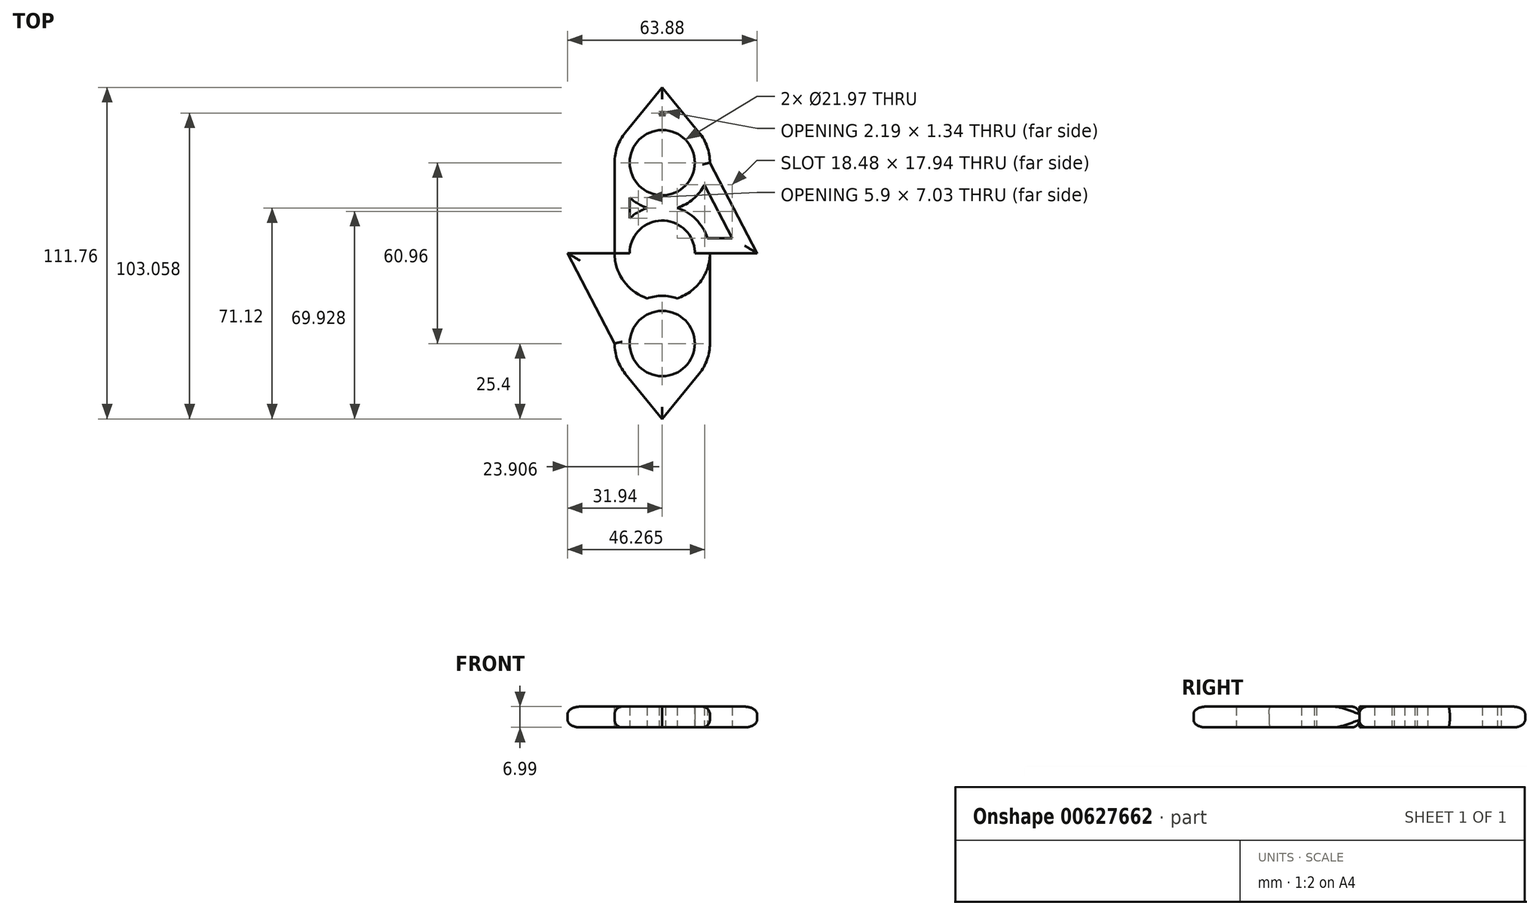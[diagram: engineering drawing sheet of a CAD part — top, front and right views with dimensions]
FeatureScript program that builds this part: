
annotation { "Feature Type Name" : "Feature", "Feature Type Description" : "" }
export const myFeature = defineFeature(function(context is Context, id is Id, definition is map)
    precondition{}
    {
        {
            var Q0;
            Q0=qCreatedBy(makeId("Top.planeOp"),FACE);
            var sketch = newSketch(context, id + "F0", { "sketchPlane" : qUnion([Q0])});
            skCircle(sketch, "E0", {"center": v(0, 0) * mm, "radius": 10.99 * mm});
            skLineSegment(sketch, "E1", {"start": v(0, 0) * mm, "end": v(0, 30.48) * mm});
            skLineSegment(sketch, "E2", {"start": v(0, 0) * mm, "end": v(0, -30.48) * mm});
            skCircle(sketch, "E3", {"center": v(0, -30.48) * mm, "radius": 10.99 * mm});
            skCircle(sketch, "E4", {"center": v(0, 30.48) * mm, "radius": 10.99 * mm});
            skCircle(sketch, "E5", {"center": v(0, 30.48) * mm, "radius": 16.07 * mm});
            skCircle(sketch, "E6", {"center": v(0, 0) * mm, "radius": 16.07 * mm});
            skCircle(sketch, "E7", {"center": v(0, -30.48) * mm, "radius": 16.07 * mm});
            skLineSegment(sketch, "E8", {"start": v(-16.07, 30.48) * mm, "end": v(-16.07, 0) * mm});
            skLineSegment(sketch, "E9", {"start": v(-16.07, 0) * mm, "end": v(-16.07, -30.48) * mm});
            skLineSegment(sketch, "E10", {"start": v(-16.07, 0) * mm, "end": v(16.07, 0) * mm});
            skLineSegment(sketch, "E11", {"start": v(-16.07, 30.48) * mm, "end": v(0, 30.48) * mm});
            skLineSegment(sketch, "E12", {"start": v(0, 30.48) * mm, "end": v(16.07, 30.48) * mm});
            skLineSegment(sketch, "E13", {"start": v(16.07, 30.48) * mm, "end": v(16.07, -30.48) * mm});
            skLineSegment(sketch, "E14", {"start": v(16.07, -30.48) * mm, "end": v(-16.07, -30.48) * mm});
            skLineSegment(sketch, "E15", {"start": v(-16.07, 0) * mm, "end": v(-31.94, 0) * mm});
            skLineSegment(sketch, "E16", {"start": v(-31.94, 0) * mm, "end": v(-16.07, -30.48) * mm});
            skLineSegment(sketch, "E17", {"start": v(16.07, 0) * mm, "end": v(31.94, 0) * mm});
            skLineSegment(sketch, "E18", {"start": v(31.94, 0) * mm, "end": v(16.07, 30.48) * mm});
            skLineSegment(sketch, "E19", {"start": v(0, 30.48) * mm, "end": v(0, 55.88) * mm});
            skLineSegment(sketch, "E20", {"start": v(0, -30.48) * mm, "end": v(0, -55.88) * mm});
            skLineSegment(sketch, "E21", {"start": v(0, 55.88) * mm, "end": v(-12.44, 40.64) * mm});
            skLineSegment(sketch, "E22", {"start": v(0, 55.88) * mm, "end": v(12.44, 40.64) * mm});
            skLineSegment(sketch, "E23", {"start": v(0, -55.88) * mm, "end": v(12.44, -40.64) * mm});
            skLineSegment(sketch, "E24", {"start": v(0, -55.88) * mm, "end": v(-12.44, -40.64) * mm});
            skSolve(sketch);
        }
        {
            var Q0;
            Q0=makeQuery(id+"F0.imprint","IMPRINT",FACE,{"disambiguationData":[TD([[makeQuery(id+"F0.imprint","IMPRINT",EDGE,{"derivedFrom":sQuery(id+"F0.wireOp",EDGE,"E9")}),-1.0]])]});
            var Q1;
            {var subQ0=sQuery(id+"F0.wireOp",EDGE,"E17");Q1=makeQuery(id+"F0.imprint","IMPRINT",FACE,{"disambiguationData":[TD([[makeQuery(id+"F0.imprint","IMPRINT",EDGE,{"derivedFrom":subQ0}),1.0]])]});}
            var Q2;
            {var subQ0=sQuery(id+"F0.wireOp",EDGE,"E22");Q2=makeQuery(id+"F0.imprint","IMPRINT",FACE,{"disambiguationData":[TD([[makeQuery(id+"F0.imprint","IMPRINT",EDGE,{"derivedFrom":subQ0}),-1.0]])]});}
            var Q3;
            {var subQ0=sQuery(id+"F0.wireOp",EDGE,"E21");Q3=makeQuery(id+"F0.imprint","IMPRINT",FACE,{"disambiguationData":[TD([[makeQuery(id+"F0.imprint","IMPRINT",EDGE,{"derivedFrom":subQ0}),1.0]])]});}
            var Q4;
            {var subQ0=sQuery(id+"F0.wireOp",EDGE,"E8");Q4=makeQuery(id+"F0.imprint","IMPRINT",FACE,{"disambiguationData":[TD([[makeQuery(id+"F0.imprint","IMPRINT",EDGE,{"derivedFrom":subQ0}),1.0]])]});}
            var Q5;
            {var subQ0=sQuery(id+"F0.wireOp",EDGE,"E24");Q5=makeQuery(id+"F0.imprint","IMPRINT",FACE,{"disambiguationData":[TD([[makeQuery(id+"F0.imprint","IMPRINT",EDGE,{"derivedFrom":subQ0}),-1.0]])]});}
            var Q6;
            {var subQ0=sQuery(id+"F0.wireOp",EDGE,"E23");Q6=makeQuery(id+"F0.imprint","IMPRINT",FACE,{"disambiguationData":[TD([[makeQuery(id+"F0.imprint","IMPRINT",EDGE,{"derivedFrom":subQ0}),1.0]])]});}
            var Q7;
            {var subQ1=sQuery(id+"F0.wireOp",EDGE,"E5");var subQ3=sQuery(id+"F0.wireOp",EDGE,"E6");var subQ4=makeQuery(id+"F0.imprint","INTERSECT",VERTEX,{"disambiguationData":[OD(1.0)],"derivedFrom":[subQ1,subQ3]});Q7=makeQuery(id+"F0.imprint","IMPRINT",FACE,{"disambiguationData":[TD([[makeQuery(id+"F0.imprint","IMPRINT",EDGE,{"disambiguationData":[TD([[subQ4,-1.0]])],"derivedFrom":subQ1}),-1.0]])]});}
            var Q8;
            {var subQ0=sQuery(id+"F0.wireOp",EDGE,"E9");Q8=makeQuery(id+"F0.imprint","IMPRINT",FACE,{"disambiguationData":[TD([[makeQuery(id+"F0.imprint","IMPRINT",EDGE,{"derivedFrom":subQ0}),1.0]])]});}
            var Q9;
            {var subQ4=sQuery(id+"F0.wireOp",EDGE,"E14");var subQ6=sQuery(id+"F0.wireOp",EDGE,"E3");var subQ7=makeQuery(id+"F0.imprint","INTERSECT",VERTEX,{"disambiguationData":[OD(1.0)],"derivedFrom":[subQ6,subQ4]});Q9=makeQuery(id+"F0.imprint","IMPRINT",FACE,{"disambiguationData":[TD([[makeQuery(id+"F0.imprint","IMPRINT",EDGE,{"disambiguationData":[TD([[subQ7,-1.0]])],"derivedFrom":subQ6}),-1.0]])]});}
            var Q10;
            {var subQ0=sQuery(id+"F0.wireOp",EDGE,"E14");var subQ3=sQuery(id+"F0.wireOp",EDGE,"E3");var subQ4=makeQuery(id+"F0.imprint","INTERSECT",VERTEX,{"disambiguationData":[OD(0.0)],"derivedFrom":[subQ3,subQ0]});Q10=makeQuery(id+"F0.imprint","IMPRINT",FACE,{"disambiguationData":[TD([[makeQuery(id+"F0.imprint","IMPRINT",EDGE,{"disambiguationData":[TD([[subQ4,1.0]])],"derivedFrom":subQ3}),-1.0]])]});}
            var Q11;
            {var subQ3=sQuery(id+"F0.wireOp",EDGE,"E4");var subQ6=sQuery(id+"F0.wireOp",EDGE,"E19");var subQ8=makeQuery(id+"F0.imprint","INTERSECT",VERTEX,{"derivedFrom":[subQ3,subQ6]});Q11=makeQuery(id+"F0.imprint","IMPRINT",FACE,{"disambiguationData":[TD([[makeQuery(id+"F0.imprint","IMPRINT",EDGE,{"disambiguationData":[TD([[subQ8,1.0]])],"derivedFrom":subQ3}),-1.0]])]});}
            var Q12;
            {var subQ3=sQuery(id+"F0.wireOp",EDGE,"E4");var subQ5=sQuery(id+"F0.wireOp",EDGE,"E19");var subQ6=makeQuery(id+"F0.imprint","INTERSECT",VERTEX,{"derivedFrom":[subQ3,subQ5]});Q12=makeQuery(id+"F0.imprint","IMPRINT",FACE,{"disambiguationData":[TD([[makeQuery(id+"F0.imprint","IMPRINT",EDGE,{"disambiguationData":[TD([[subQ6,-1.0]])],"derivedFrom":subQ3}),-1.0]])]});}
            var Q13;
            {var subQ1=sQuery(id+"F0.wireOp",EDGE,"E1");var subQ7=sQuery(id+"F0.wireOp",EDGE,"E0");var subQ8=makeQuery(id+"F0.imprint","INTERSECT",VERTEX,{"derivedFrom":[subQ7,subQ1]});Q13=makeQuery(id+"F0.imprint","IMPRINT",FACE,{"disambiguationData":[TD([[makeQuery(id+"F0.imprint","IMPRINT",EDGE,{"disambiguationData":[TD([[subQ8,1.0]])],"derivedFrom":subQ7}),-1.0]])]});}
            var Q14;
            {var subQ5=sQuery(id+"F0.wireOp",EDGE,"E1");var subQ7=sQuery(id+"F0.wireOp",EDGE,"E0");var subQ8=makeQuery(id+"F0.imprint","INTERSECT",VERTEX,{"derivedFrom":[subQ7,subQ5]});Q14=makeQuery(id+"F0.imprint","IMPRINT",FACE,{"disambiguationData":[TD([[makeQuery(id+"F0.imprint","IMPRINT",EDGE,{"disambiguationData":[TD([[subQ8,-1.0]])],"derivedFrom":subQ7}),-1.0]])]});}
            var Q15;
            {var subQ0=sQuery(id+"F0.wireOp",EDGE,"E10");var subQ7=sQuery(id+"F0.wireOp",EDGE,"E0");var subQ9=makeQuery(id+"F0.imprint","INTERSECT",VERTEX,{"disambiguationData":[OD(1.0)],"derivedFrom":[subQ7,subQ0]});Q15=makeQuery(id+"F0.imprint","IMPRINT",FACE,{"disambiguationData":[TD([[makeQuery(id+"F0.imprint","IMPRINT",EDGE,{"disambiguationData":[TD([[subQ9,-1.0]])],"derivedFrom":subQ7}),-1.0]])]});}
            var Q16;
            {var subQ5=sQuery(id+"F0.wireOp",EDGE,"E10");var subQ7=sQuery(id+"F0.wireOp",EDGE,"E0");var subQ9=makeQuery(id+"F0.imprint","INTERSECT",VERTEX,{"disambiguationData":[OD(0.0)],"derivedFrom":[subQ7,subQ5]});Q16=makeQuery(id+"F0.imprint","IMPRINT",FACE,{"disambiguationData":[TD([[makeQuery(id+"F0.imprint","IMPRINT",EDGE,{"disambiguationData":[TD([[subQ9,1.0]])],"derivedFrom":subQ7}),-1.0]])]});}
            var Q17;
            {var subQ3=sQuery(id+"F0.wireOp",EDGE,"E6");var subQ6=sQuery(id+"F0.wireOp",EDGE,"E1");var subQ9=makeQuery(id+"F0.imprint","INTERSECT",VERTEX,{"derivedFrom":[subQ6,subQ3]});Q17=makeQuery(id+"F0.imprint","IMPRINT",FACE,{"disambiguationData":[TD([[makeQuery(id+"F0.imprint","IMPRINT",EDGE,{"disambiguationData":[TD([[subQ9,-1.0]])],"derivedFrom":subQ6}),1.0]])]});}
            var Q18;
            {var subQ3=sQuery(id+"F0.wireOp",EDGE,"E6");var subQ5=sQuery(id+"F0.wireOp",EDGE,"E1");var subQ6=makeQuery(id+"F0.imprint","INTERSECT",VERTEX,{"derivedFrom":[subQ5,subQ3]});Q18=makeQuery(id+"F0.imprint","IMPRINT",FACE,{"disambiguationData":[TD([[makeQuery(id+"F0.imprint","IMPRINT",EDGE,{"disambiguationData":[TD([[subQ6,-1.0]])],"derivedFrom":subQ5}),-1.0]])]});}
            var Q19;
            {var subQ3=sQuery(id+"F0.wireOp",EDGE,"E6");var subQ5=sQuery(id+"F0.wireOp",EDGE,"E2");var subQ6=makeQuery(id+"F0.imprint","INTERSECT",VERTEX,{"derivedFrom":[subQ5,subQ3]});Q19=makeQuery(id+"F0.imprint","IMPRINT",FACE,{"disambiguationData":[TD([[makeQuery(id+"F0.imprint","IMPRINT",EDGE,{"disambiguationData":[TD([[subQ6,-1.0]])],"derivedFrom":subQ5}),1.0]])]});}
            var Q20;
            {var subQ3=sQuery(id+"F0.wireOp",EDGE,"E6");var subQ5=sQuery(id+"F0.wireOp",EDGE,"E2");var subQ6=makeQuery(id+"F0.imprint","INTERSECT",VERTEX,{"derivedFrom":[subQ5,subQ3]});Q20=makeQuery(id+"F0.imprint","IMPRINT",FACE,{"disambiguationData":[TD([[makeQuery(id+"F0.imprint","IMPRINT",EDGE,{"disambiguationData":[TD([[subQ6,-1.0]])],"derivedFrom":subQ5}),-1.0]])]});}
            var Q21;
            {var subQ0=sQuery(id+"F0.wireOp",EDGE,"E7");var subQ1=sQuery(id+"F0.wireOp",EDGE,"E2");var subQ2=makeQuery(id+"F0.imprint","INTERSECT",VERTEX,{"derivedFrom":[subQ1,subQ0]});Q21=makeQuery(id+"F0.imprint","IMPRINT",FACE,{"disambiguationData":[TD([[makeQuery(id+"F0.imprint","IMPRINT",EDGE,{"disambiguationData":[TD([[subQ2,-1.0]])],"derivedFrom":subQ1}),1.0]])]});}
            var Q22;
            {var subQ0=sQuery(id+"F0.wireOp",EDGE,"E7");var subQ1=sQuery(id+"F0.wireOp",EDGE,"E2");var subQ2=makeQuery(id+"F0.imprint","INTERSECT",VERTEX,{"derivedFrom":[subQ1,subQ0]});Q22=makeQuery(id+"F0.imprint","IMPRINT",FACE,{"disambiguationData":[TD([[makeQuery(id+"F0.imprint","IMPRINT",EDGE,{"disambiguationData":[TD([[subQ2,-1.0]])],"derivedFrom":subQ1}),-1.0]])]});}
            var Q23;
            {var subQ1=sQuery(id+"F0.wireOp",EDGE,"E6");var subQ3=sQuery(id+"F0.wireOp",EDGE,"E7");var subQ4=makeQuery(id+"F0.imprint","INTERSECT",VERTEX,{"disambiguationData":[OD(1.0)],"derivedFrom":[subQ1,subQ3]});Q23=makeQuery(id+"F0.imprint","IMPRINT",FACE,{"disambiguationData":[TD([[makeQuery(id+"F0.imprint","IMPRINT",EDGE,{"disambiguationData":[TD([[subQ4,1.0]])],"derivedFrom":subQ3}),-1.0]])]});}
            var Q24;
            {var subQ0=sQuery(id+"F0.wireOp",EDGE,"E5");var subQ1=sQuery(id+"F0.wireOp",EDGE,"E1");var subQ2=makeQuery(id+"F0.imprint","INTERSECT",VERTEX,{"derivedFrom":[subQ1,subQ0]});Q24=makeQuery(id+"F0.imprint","IMPRINT",FACE,{"disambiguationData":[TD([[makeQuery(id+"F0.imprint","IMPRINT",EDGE,{"disambiguationData":[TD([[subQ2,-1.0]])],"derivedFrom":subQ1}),-1.0]])]});}
            var Q25;
            {var subQ0=sQuery(id+"F0.wireOp",EDGE,"E5");var subQ1=sQuery(id+"F0.wireOp",EDGE,"E1");var subQ2=makeQuery(id+"F0.imprint","INTERSECT",VERTEX,{"derivedFrom":[subQ1,subQ0]});Q25=makeQuery(id+"F0.imprint","IMPRINT",FACE,{"disambiguationData":[TD([[makeQuery(id+"F0.imprint","IMPRINT",EDGE,{"disambiguationData":[TD([[subQ2,-1.0]])],"derivedFrom":subQ1}),1.0]])]});}
            extrude(context, id + "F1", {"entities" : qUnion([Q0, Q1, Q2, Q3, Q4, Q5, Q6, Q7, Q8, Q9, Q10, Q11, Q12, Q13, Q14, Q15, Q16, Q17, Q18, Q19, Q20, Q21, Q22, Q23, Q24, Q25]), "depth" : 7 * mm, "offsetDistance" : 25.4 * mm});
        }
        {
            var Q0;
            Q0=makeQuery(id+"F1.opExtrude","CAP_FACE",FACE,{"disambiguationData":[OSD([sQuery(id+"F0.wireOp",EDGE,"E0"),sQuery(id+"F0.wireOp",EDGE,"E3"),sQuery(id+"F0.wireOp",EDGE,"E4"),sQuery(id+"F0.wireOp",EDGE,"E5"),sQuery(id+"F0.wireOp",EDGE,"E7"),sQuery(id+"F0.wireOp",EDGE,"E8"),sQuery(id+"F0.wireOp",EDGE,"E13"),sQuery(id+"F0.wireOp",EDGE,"E15"),sQuery(id+"F0.wireOp",EDGE,"E16"),sQuery(id+"F0.wireOp",EDGE,"E17"),sQuery(id+"F0.wireOp",EDGE,"E18"),sQuery(id+"F0.wireOp",EDGE,"E21"),sQuery(id+"F0.wireOp",EDGE,"E22"),sQuery(id+"F0.wireOp",EDGE,"E23"),sQuery(id+"F0.wireOp",EDGE,"E24")])],"isStart":false});
            var Q1;
            Q1=makeQuery(id+"F1.opExtrude","CAP_FACE",FACE,{"disambiguationData":[OSD([sQuery(id+"F0.wireOp",EDGE,"E0"),sQuery(id+"F0.wireOp",EDGE,"E3"),sQuery(id+"F0.wireOp",EDGE,"E4"),sQuery(id+"F0.wireOp",EDGE,"E5"),sQuery(id+"F0.wireOp",EDGE,"E7"),sQuery(id+"F0.wireOp",EDGE,"E8"),sQuery(id+"F0.wireOp",EDGE,"E13"),sQuery(id+"F0.wireOp",EDGE,"E15"),sQuery(id+"F0.wireOp",EDGE,"E16"),sQuery(id+"F0.wireOp",EDGE,"E17"),sQuery(id+"F0.wireOp",EDGE,"E18"),sQuery(id+"F0.wireOp",EDGE,"E21"),sQuery(id+"F0.wireOp",EDGE,"E22"),sQuery(id+"F0.wireOp",EDGE,"E23"),sQuery(id+"F0.wireOp",EDGE,"E24")])],"isStart":true});
            shell(context, id + "F2", {"entities" : qUnion([Q0, Q1]), "thickness" : 5.08 * mm});
        }
        {
            var Q0;
            Q0=makeQuery(id+"F1.opExtrude","CAP_EDGE",EDGE,{"disambiguationData":[OSD([sQuery(id+"F0.wireOp",EDGE,"E16")])],"isStart":false});
            var Q1;
            Q1=makeQuery(id+"F1.opExtrude","CAP_EDGE",EDGE,{"disambiguationData":[OSD([sQuery(id+"F0.wireOp",EDGE,"E15")])],"isStart":false});
            var Q2;
            Q2=makeQuery(id+"F1.opExtrude","CAP_EDGE",EDGE,{"disambiguationData":[OSD([sQuery(id+"F0.wireOp",EDGE,"E8")])],"isStart":false});
            var Q3;
            Q3=makeQuery(id+"F1.opExtrude","CAP_EDGE",EDGE,{"disambiguationData":[OSD([sQuery(id+"F0.wireOp",EDGE,"E22")])],"isStart":false});
            var Q4;
            Q4=makeQuery(id+"F1.opExtrude","CAP_EDGE",EDGE,{"disambiguationData":[OSD([sQuery(id+"F0.wireOp",EDGE,"E17")])],"isStart":false});
            var Q5;
            Q5=makeQuery(id+"F1.opExtrude","CAP_EDGE",EDGE,{"disambiguationData":[OSD([sQuery(id+"F0.wireOp",EDGE,"E13")])],"isStart":false});
            var Q6;
            Q6=makeQuery(id+"F1.opExtrude","CAP_EDGE",EDGE,{"disambiguationData":[OSD([sQuery(id+"F0.wireOp",EDGE,"E23")])],"isStart":false});
            var Q7;
            Q7=makeQuery(id+"F1.opExtrude","CAP_EDGE",EDGE,{"disambiguationData":[OSD([sQuery(id+"F0.wireOp",EDGE,"E24")])],"isStart":false});
            var Q8;
            {var subQ0=sQuery(id+"F0.wireOp",EDGE,"E5");Q8=makeQuery(id+"F1.opExtrude","CAP_EDGE",EDGE,{"disambiguationData":[OSD([subQ0]),TDD([makeQuery(id+"F0.imprint","IMPRINT",EDGE,{"disambiguationData":[TD([[makeQuery(id+"F0.imprint","INTERSECT",VERTEX,{"derivedFrom":[subQ0,sQuery(id+"F0.wireOp",EDGE,"E22")]}),1.0]])],"derivedFrom":subQ0})])],"isStart":false});}
            var Q9;
            Q9=makeQuery(id+"F1.opExtrude","CAP_EDGE",EDGE,{"disambiguationData":[OSD([sQuery(id+"F0.wireOp",EDGE,"E21")])],"isStart":false});
            var Q10;
            {var subQ0=sQuery(id+"F0.wireOp",EDGE,"E5");Q10=makeQuery(id+"F1.opExtrude","CAP_EDGE",EDGE,{"disambiguationData":[OSD([subQ0]),TDD([makeQuery(id+"F0.imprint","IMPRINT",EDGE,{"disambiguationData":[TD([[makeQuery(id+"F0.imprint","INTERSECT",VERTEX,{"derivedFrom":[subQ0,sQuery(id+"F0.wireOp",EDGE,"E21")]}),-1.0]])],"derivedFrom":subQ0})])],"isStart":false});}
            var Q11;
            Q11=makeQuery(id+"F1.opExtrude","CAP_EDGE",EDGE,{"disambiguationData":[OSD([sQuery(id+"F0.wireOp",EDGE,"E18")])],"isStart":false});
            fillet(context, id + "F3", {"entities" : qUnion([Q0, Q1, Q2, Q3, Q4, Q5, Q6, Q7, Q8, Q9, Q10, Q11]), "radius" : 2.54 * mm, "tangentPropagation" : true, "allowEdgeOverflow" : false});
        }
        {
            var Q0;
            Q0=makeQuery(id+"F1.opExtrude","CAP_EDGE",EDGE,{"disambiguationData":[OSD([sQuery(id+"F0.wireOp",EDGE,"E13")])],"isStart":true});
            var Q1;
            {var subQ0=sQuery(id+"F0.wireOp",EDGE,"E7");Q1=makeQuery(id+"F1.opExtrude","CAP_EDGE",EDGE,{"disambiguationData":[OSD([subQ0]),TDD([makeQuery(id+"F0.imprint","IMPRINT",EDGE,{"disambiguationData":[TD([[makeQuery(id+"F0.imprint","INTERSECT",VERTEX,{"derivedFrom":[subQ0,sQuery(id+"F0.wireOp",EDGE,"E24")]}),1.0]])],"derivedFrom":subQ0})])],"isStart":true});}
            var Q2;
            Q2=makeQuery(id+"F1.opExtrude","CAP_EDGE",EDGE,{"disambiguationData":[OSD([sQuery(id+"F0.wireOp",EDGE,"E16")])],"isStart":true});
            var Q3;
            Q3=makeQuery(id+"F1.opExtrude","CAP_EDGE",EDGE,{"disambiguationData":[OSD([sQuery(id+"F0.wireOp",EDGE,"E15")])],"isStart":true});
            var Q4;
            Q4=makeQuery(id+"F1.opExtrude","CAP_EDGE",EDGE,{"disambiguationData":[OSD([sQuery(id+"F0.wireOp",EDGE,"E8")])],"isStart":true});
            var Q5;
            Q5=makeQuery(id+"F1.opExtrude","CAP_EDGE",EDGE,{"disambiguationData":[OSD([sQuery(id+"F0.wireOp",EDGE,"E22")])],"isStart":true});
            var Q6;
            Q6=makeQuery(id+"F1.opExtrude","CAP_EDGE",EDGE,{"disambiguationData":[OSD([sQuery(id+"F0.wireOp",EDGE,"E18")])],"isStart":true});
            var Q7;
            Q7=makeQuery(id+"F1.opExtrude","CAP_EDGE",EDGE,{"disambiguationData":[OSD([sQuery(id+"F0.wireOp",EDGE,"E17")])],"isStart":true});
            fillet(context, id + "F4", {"entities" : qUnion([Q0, Q1, Q2, Q3, Q4, Q5, Q6, Q7]), "radius" : 2.54 * mm, "tangentPropagation" : true, "allowEdgeOverflow" : false});
        }
    });
